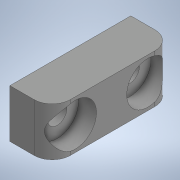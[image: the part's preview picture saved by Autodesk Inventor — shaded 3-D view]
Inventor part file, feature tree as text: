
AUTODESK INVENTOR PART (.ipt)
format: ipt  version: 2022 (Build 260153000, 153)  size: 210,432 bytes
history: native  units: mm
features: extrude x3, sketch x3, fillet x2, projected_geometry x1
ambient origin geometry x8: Origin, YZ Plane, XZ Plane, XY Plane, X Axis, Y Axis, Z Axis, Center Point
bodies: Solid1 (feature_tree)
feature tree (9):
  extrude  "Extrusion1"  Depth=3.2mm
  extrude  "Extrusion2"  Depth=8.0mm
  fillet  "Fillet1"  Radius=20.0mm
  extrude  "Extrusion3"  Depth=7.0mm
  fillet  "Fillet2"  Radius=7.0mm
  sketch  "Sketch1"  dims[d0=3.2mm d1=3.2mm]
  sketch  "Sketch2"  dims[d2=12.0mm d6=8.0mm d7=20.0mm]
  projected_geometry  "Projected Loop1"
  sketch  "Sketch3"  dims[d8=4.0mm d9=0.0mm d10=7.0mm d11=7.0mm d12=3.0mm d13=0.0mm d14=3.0mm d15=7.0mm d16=12.0mm d17=6.0mm d18=1.0mm d19=0.5mm d20=40.0mm d22=2.0mm d23=10.0mm d25=10.0mm d27=0.5mm d28=0.0mm d29=0.25mm]
